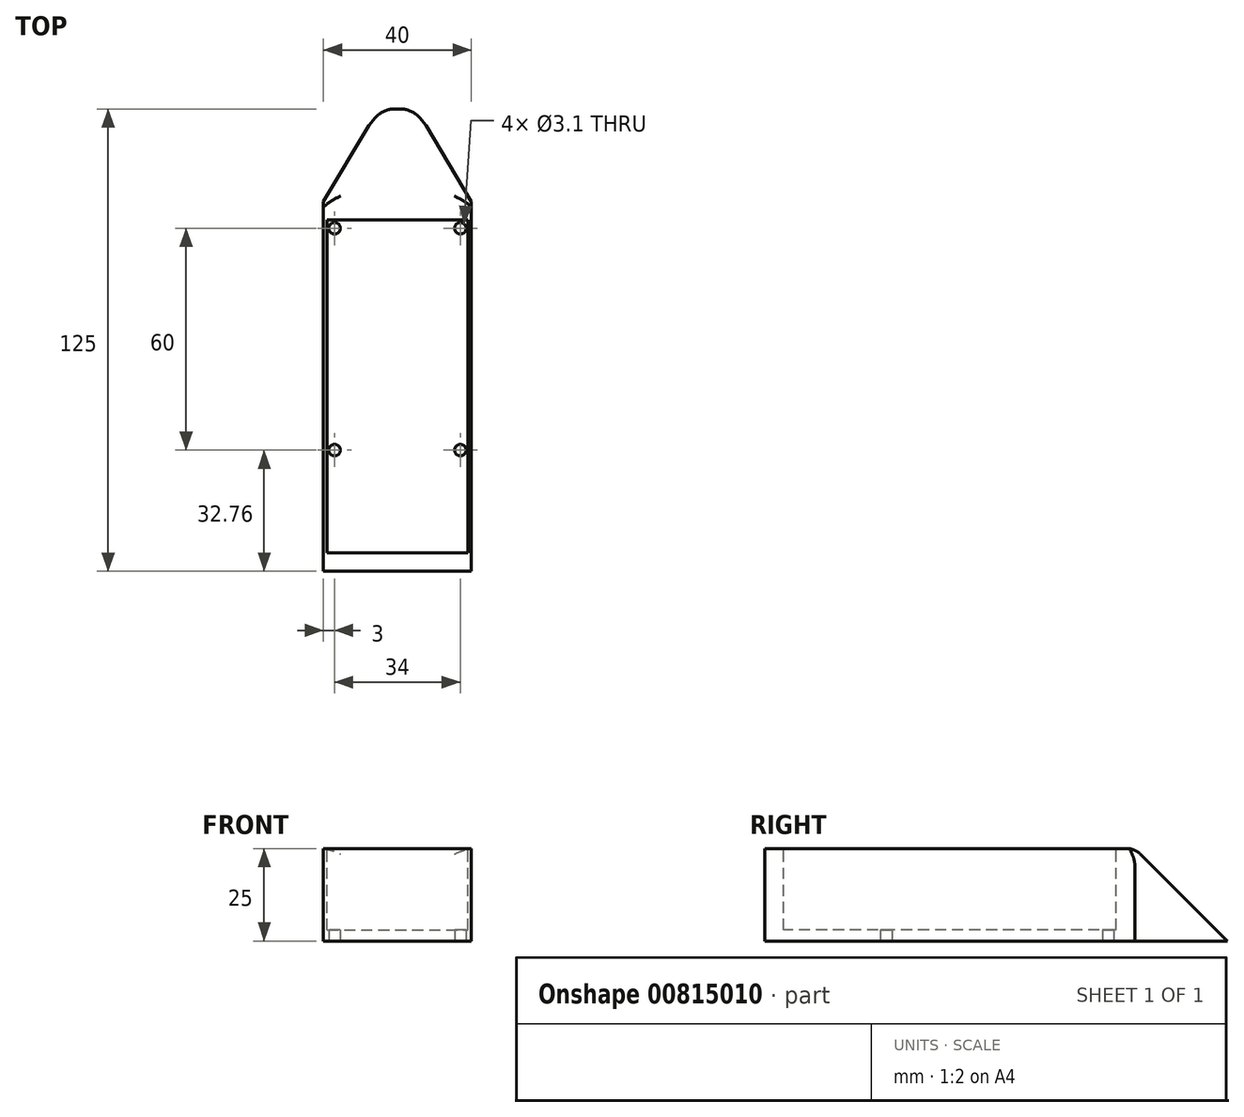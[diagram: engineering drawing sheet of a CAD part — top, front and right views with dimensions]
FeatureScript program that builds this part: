
annotation { "Feature Type Name" : "Feature", "Feature Type Description" : "" }
export const myFeature = defineFeature(function(context is Context, id is Id, definition is map)
    precondition{}
    {
        {
            var Q0;
            Q0=qCreatedBy(makeId("Top.planeOp"),FACE);
            var sketch = newSketch(context, id + "F0", { "sketchPlane" : qUnion([Q0])});
            skLineSegment(sketch, "E0.bottom", {"start": v(-20, 100) * mm, "end": v(20, 100) * mm});
            skLineSegment(sketch, "E0.top", {"start": v(-20, 0) * mm, "end": v(20, 0) * mm});
            skLineSegment(sketch, "E0.left", {"start": v(-20, 100) * mm, "end": v(-20, 0) * mm});
            skLineSegment(sketch, "E0.right", {"start": v(20, 100) * mm, "end": v(20, 0) * mm});
            skCircle(sketch, "E1", {"center": v(-17, 32.76) * mm, "radius": 1.55 * mm});
            skCircle(sketch, "E2", {"center": v(17, 32.76) * mm, "radius": 1.55 * mm});
            skCircle(sketch, "E3", {"center": v(-17, 92.76) * mm, "radius": 1.55 * mm});
            skCircle(sketch, "E4", {"center": v(17, 92.76) * mm, "radius": 1.55 * mm});
            skLineSegment(sketch, "E5.bottom", {"start": v(17, 92.76) * mm, "end": v(-17, 92.76) * mm, "construction": true});
            skLineSegment(sketch, "E5.top", {"start": v(17, 32.76) * mm, "end": v(-17, 32.76) * mm, "construction": true});
            skLineSegment(sketch, "E5.left", {"start": v(17, 92.76) * mm, "end": v(17, 32.76) * mm, "construction": true});
            skLineSegment(sketch, "E5.right", {"start": v(-17, 92.76) * mm, "end": v(-17, 32.76) * mm, "construction": true});
            skLineSegment(sketch, "E6.bottom", {"start": v(-18, 93.02) * mm, "end": v(18, 93.02) * mm, "construction": true});
            skLineSegment(sketch, "E6.top", {"start": v(-18, 3.02) * mm, "end": v(18, 3.02) * mm, "construction": true});
            skLineSegment(sketch, "E6.left", {"start": v(-18, 93.02) * mm, "end": v(-18, 3.02) * mm, "construction": true});
            skLineSegment(sketch, "E6.right", {"start": v(18, 93.02) * mm, "end": v(18, 3.02) * mm, "construction": true});
            skLineSegment(sketch, "E7", {"start": v(0, 100) * mm, "end": v(0, 0) * mm, "construction": true});
            skLineSegment(sketch, "E8", {"start": v(-20, 50) * mm, "end": v(20, 50) * mm, "construction": true});
            skSolve(sketch);
        }
        {
            var Q0;
            Q0 = qSketchRegion(id + "F0", true);
            extrude(context, id + "F1", {"entities" : qUnion([Q0]), "depth" : 25 * mm, "offsetDistance" : 25 * mm});
        }
        {
            var Q0;
            Q0=makeQuery(id+"F1.opExtrude","CAP_FACE",FACE,{"disambiguationData":[OSD([sQuery(id+"F0.wireOp",EDGE,"E0.bottom"),sQuery(id+"F0.wireOp",EDGE,"E0.top"),sQuery(id+"F0.wireOp",EDGE,"E0.left"),sQuery(id+"F0.wireOp",EDGE,"E0.right"),sQuery(id+"F0.wireOp",EDGE,"E1"),sQuery(id+"F0.wireOp",EDGE,"E2"),sQuery(id+"F0.wireOp",EDGE,"E3"),sQuery(id+"F0.wireOp",EDGE,"E4")])],"isStart":false});
            var sketch = newSketch(context, id + "F2", { "sketchPlane" : qUnion([Q0])});
            skLineSegment(sketch, "E9.bottom", {"start": v(-19, 95) * mm, "end": v(19, 95) * mm});
            skLineSegment(sketch, "E9.top", {"start": v(-19, 5) * mm, "end": v(19, 5) * mm});
            skLineSegment(sketch, "E9.left", {"start": v(-19, 95) * mm, "end": v(-19, 5) * mm});
            skLineSegment(sketch, "E9.right", {"start": v(19, 95) * mm, "end": v(19, 5) * mm});
            skSolve(sketch);
        }
        {
            var Q0;
            Q0 = qSketchRegion(id + "F2", true);
            extrude(context, id + "F3", {"entities" : qUnion([Q0]), "operationType" : NewBodyOperationType.REMOVE, "oppositeDirection" : true, "depth" : 22 * mm, "offsetDistance" : 25 * mm});
        }
        {
            var Q0;
            Q0=qCreatedBy(makeId("Top.planeOp"),FACE);
            var sketch = newSketch(context, id + "F4", { "sketchPlane" : qUnion([Q0])});
            skLineSegment(sketch, "E10", {"start": v(-20, 100) * mm, "end": v(20, 100) * mm});
            skLineSegment(sketch, "E11", {"start": v(20, 100) * mm, "end": v(5, 125) * mm});
            skLineSegment(sketch, "E12", {"start": v(5, 125) * mm, "end": v(-5, 125) * mm});
            skLineSegment(sketch, "E13", {"start": v(-5, 125) * mm, "end": v(-20, 100) * mm});
            skSolve(sketch);
        }
        {
            var Q1;
            Q1=makeQuery(id+"F1.opExtrude","SWEPT_FACE",FACE,{"disambiguationData":[OSD([sQuery(id+"F0.wireOp",EDGE,"E0.bottom")])]});
            var Q2;
            Q2=makeQuery(id+"F4.imprint","IMPRINT",FACE,{"disambiguationData":[TD([[makeQuery(id+"F4.imprint","IMPRINT",EDGE,{"derivedFrom":sQuery(id+"F4.wireOp",EDGE,"E10")}),1.0]])]});
            var Q3;
            Q3=makeQuery(id+"F1.opExtrude","CAP_VERTEX",VERTEX,{"disambiguationData":[OSD([sQuery(id+"F0.wireOp",EDGE,"E0.bottom"),sQuery(id+"F0.wireOp",EDGE,"E0.left")])],"isStart":false});
            var Q4;
            Q4=sQuery(id+"F4.wireOp",VERTEX,"E12.end");
            loft(context, id + "F5", {"operationType" : NewBodyOperationType.ADD, "sheetProfilesArray" : [{ "sheetProfileEntities" : qUnion([Q1]) }, { "sheetProfileEntities" : qUnion([Q2]) }], "matchConnections" : true, "connections" : [{ "connectionEntities" : qUnion([Q3, Q4]), "connectionEdgeQueries" : qUnion([]), "connectionEdgeParameters" : [] }]});
        }
        {
            var Q0;
            Q0=makeQuery(id+"F5.opLoft","SWEPT_EDGE",EDGE,{"disambiguationData":[OSD([sQuery(id+"F0.wireOp",EDGE,"E0.bottom"),sQuery(id+"F0.wireOp",EDGE,"E0.left"),sQuery(id+"F4.wireOp",EDGE,"E12"),sQuery(id+"F4.wireOp",EDGE,"E13")])]});
            var Q1;
            Q1=makeQuery(id+"F5.opLoft","SWEPT_EDGE",EDGE,{"disambiguationData":[OSD([sQuery(id+"F0.wireOp",EDGE,"E0.bottom"),sQuery(id+"F0.wireOp",EDGE,"E0.right"),sQuery(id+"F4.wireOp",EDGE,"E11"),sQuery(id+"F4.wireOp",EDGE,"E12")])]});
            var Q2;
            {var subQ0=sQuery(id+"F0.wireOp",EDGE,"E0.bottom");Q2=makeQuery(id+"F5.boolean.opBoolean","MERGE",EDGE,{"derivedFrom":[makeQuery(id+"F1.opExtrude","CAP_EDGE",EDGE,{"disambiguationData":[OSD([subQ0])],"isStart":false}),makeQuery(id+"F5.opLoft","MID_CAP_EDGE",EDGE,{"disambiguationData":[OSD([subQ0,sQuery(id+"F0.wireOp",EDGE,"E0.left"),sQuery(id+"F0.wireOp",EDGE,"E0.right")])],"capPos":0.0})]});}
            fillet(context, id + "F6", {"entities" : qUnion([Q0, Q1, Q2]), "radius" : 5 * mm, "tangentPropagation" : true, "allowEdgeOverflow" : false});
        }
    });
